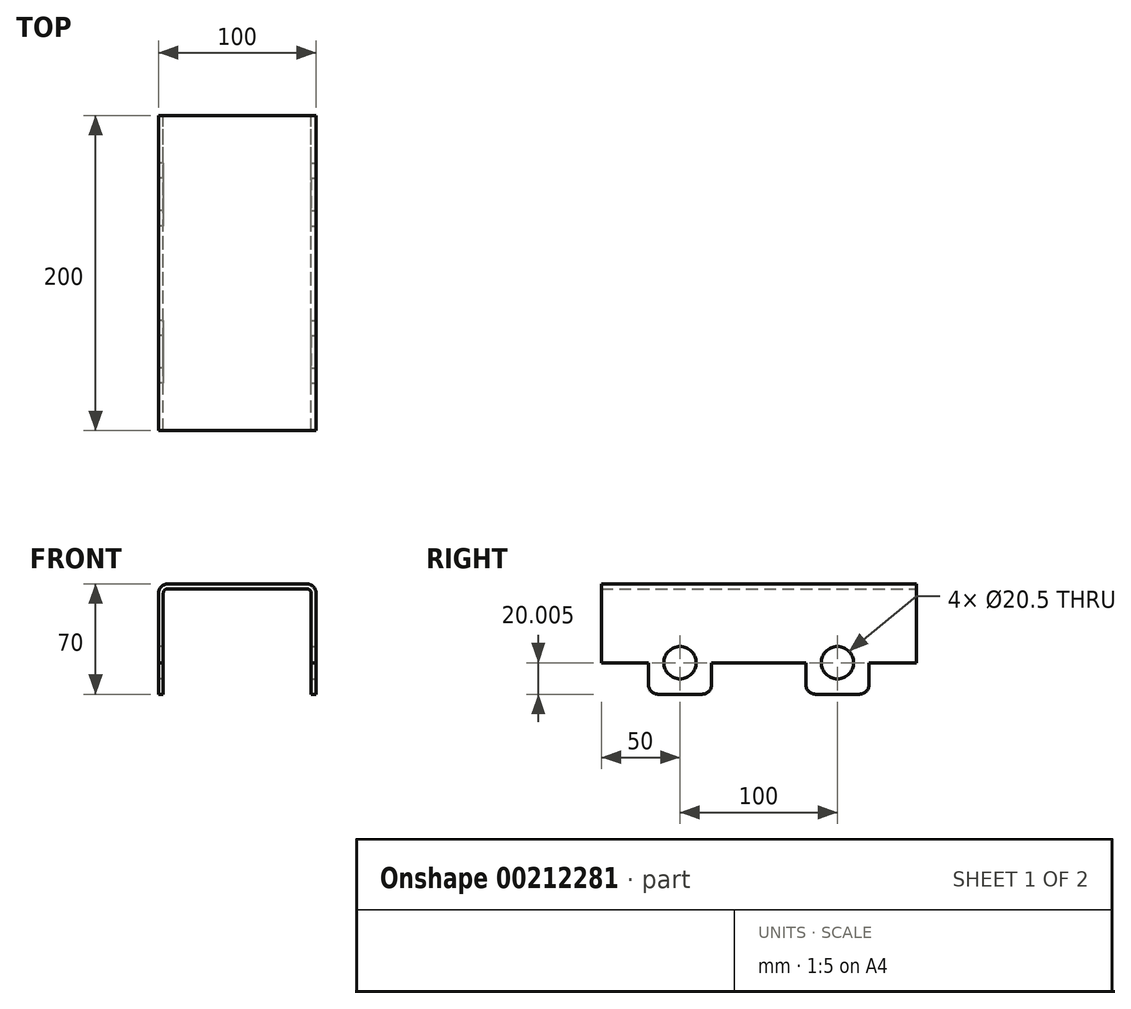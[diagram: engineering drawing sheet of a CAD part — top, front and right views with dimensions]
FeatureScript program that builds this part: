
annotation { "Feature Type Name" : "Feature", "Feature Type Description" : "" }
export const myFeature = defineFeature(function(context is Context, id is Id, definition is map)
    precondition{}
    {
        {
            var Q0;
            Q0=qCreatedBy(makeId("Front.planeOp"),FACE);
            var sketch = newSketch(context, id + "F0", { "sketchPlane" : qUnion([Q0])});
            skLineSegment(sketch, "E0", {"start": v(0, 20.85) * mm, "end": v(44, 20.85) * mm});
            skLineSegment(sketch, "E1", {"start": v(47, 17.85) * mm, "end": v(47, -26.15) * mm});
            skLineSegment(sketch, "E2", {"start": v(47, -26.15) * mm, "end": v(50, -26.15) * mm});
            skLineSegment(sketch, "E3", {"start": v(50, -26.15) * mm, "end": v(50, 17.85) * mm});
            skLineSegment(sketch, "E4", {"start": v(44, 23.85) * mm, "end": v(0, 23.85) * mm});
            skLineSegment(sketch, "E5", {"start": v(0, 20.85) * mm, "end": v(0, 23.85) * mm});
            skPoint(sketch, "E6.visualSharp", {"position": v(47, 20.85) * mm});
            skArc(sketch, "E6.filletArc", {"start": v(47, 17.85) * mm, "mid": v(46.12, 19.98) * mm, "end": v(44, 20.85) * mm});
            skPoint(sketch, "E7.visualSharp", {"position": v(50, 23.85) * mm});
            skArc(sketch, "E7.filletArc", {"start": v(50, 17.85) * mm, "mid": v(48.24, 22.1) * mm, "end": v(44, 23.85) * mm});
            skLineSegment(sketch, "E8.MirrorCS", {"start": v(-47, -26.15) * mm, "end": v(-50, -26.15) * mm});
            skArc(sketch, "E9.MirrorCS", {"start": v(-47, 17.85) * mm, "mid": v(-46.12, 19.98) * mm, "end": v(-44, 20.85) * mm});
            skLineSegment(sketch, "E10.MirrorCS", {"start": v(0, 20.85) * mm, "end": v(-44, 20.85) * mm});
            skLineSegment(sketch, "E11.MirrorCS", {"start": v(-47, 17.85) * mm, "end": v(-47, -26.15) * mm});
            skLineSegment(sketch, "E12.MirrorCS", {"start": v(-44, 23.85) * mm, "end": v(0, 23.85) * mm});
            skPoint(sketch, "E13.MirrorP", {"position": v(-47, 20.85) * mm});
            skPoint(sketch, "E14.MirrorP", {"position": v(-50, 23.85) * mm});
            skArc(sketch, "E15.MirrorCS", {"start": v(-50, 17.85) * mm, "mid": v(-48.24, 22.1) * mm, "end": v(-44, 23.85) * mm});
            skLineSegment(sketch, "E16.MirrorCS", {"start": v(-50, -26.15) * mm, "end": v(-50, 17.85) * mm});
            skSolve(sketch);
        }
        {
            var Q0;
            Q0=makeQuery(id+"F0.imprint","IMPRINT",FACE,{"disambiguationData":[TD([[makeQuery(id+"F0.imprint","IMPRINT",EDGE,{"derivedFrom":sQuery(id+"F0.wireOp",EDGE,"E0")}),1.0]])]});
            var Q1;
            Q1=makeQuery(id+"F0.imprint","IMPRINT",FACE,{"disambiguationData":[TD([[makeQuery(id+"F0.imprint","IMPRINT",EDGE,{"derivedFrom":sQuery(id+"F0.wireOp",EDGE,"E5")}),1.0]])]});
            extrude(context, id + "F1", {"entities" : qUnion([Q0, Q1]), "depth" : 200 * mm});
        }
        {
            var Q0;
            Q0=makeQuery(id+"F1.opExtrude","SWEPT_FACE",FACE,{"disambiguationData":[OSD([sQuery(id+"F0.wireOp",EDGE,"E3")])]});
            var sketch = newSketch(context, id + "F2", { "sketchPlane" : qUnion([Q0])});
            skLineSegment(sketch, "E17.bottom", {"start": v(-170, -26.15) * mm, "end": v(-130, -26.15) * mm});
            skLineSegment(sketch, "E17.top", {"start": v(-164, -46.15) * mm, "end": v(-136, -46.15) * mm});
            skLineSegment(sketch, "E17.left", {"start": v(-170, -26.15) * mm, "end": v(-170, -40.15) * mm});
            skLineSegment(sketch, "E17.right", {"start": v(-130, -26.15) * mm, "end": v(-130, -40.15) * mm});
            skLineSegment(sketch, "E18.bottom", {"start": v(-70, -26.15) * mm, "end": v(-30, -26.15) * mm});
            skLineSegment(sketch, "E18.top", {"start": v(-64, -46.15) * mm, "end": v(-36, -46.15) * mm});
            skLineSegment(sketch, "E18.left", {"start": v(-70, -26.15) * mm, "end": v(-70, -40.15) * mm});
            skLineSegment(sketch, "E18.right", {"start": v(-30, -26.15) * mm, "end": v(-30, -40.15) * mm});
            skPoint(sketch, "E19.visualSharp", {"position": v(-170, -46.15) * mm});
            skArc(sketch, "E19.filletArc", {"start": v(-170, -40.15) * mm, "mid": v(-168.24, -44.39) * mm, "end": v(-164, -46.15) * mm});
            skPoint(sketch, "E20.visualSharp", {"position": v(-130, -46.15) * mm});
            skArc(sketch, "E20.filletArc", {"start": v(-136, -46.15) * mm, "mid": v(-131.76, -44.39) * mm, "end": v(-130, -40.15) * mm});
            skPoint(sketch, "E21.visualSharp", {"position": v(-70, -46.15) * mm});
            skArc(sketch, "E21.filletArc", {"start": v(-70, -40.15) * mm, "mid": v(-68.24, -44.39) * mm, "end": v(-64, -46.15) * mm});
            skPoint(sketch, "E22.visualSharp", {"position": v(-30, -46.15) * mm});
            skArc(sketch, "E22.filletArc", {"start": v(-36, -46.15) * mm, "mid": v(-31.76, -44.39) * mm, "end": v(-30, -40.15) * mm});
            skCircle(sketch, "E23", {"center": v(-150, -26.15) * mm, "radius": 10.25 * mm});
            skCircle(sketch, "E24", {"center": v(-50, -26.15) * mm, "radius": 10.25 * mm});
            skSolve(sketch);
        }
        {
            var Q0;
            Q0=makeQuery(id+"F2.imprint","IMPRINT",FACE,{"disambiguationData":[TD([[makeQuery(id+"F2.imprint","IMPRINT",EDGE,{"derivedFrom":sQuery(id+"F2.wireOp",EDGE,"E17.bottom")}),-1.0]])]});
            var Q1;
            Q1=makeQuery(id+"F2.imprint","IMPRINT",FACE,{"disambiguationData":[TD([[makeQuery(id+"F2.imprint","IMPRINT",EDGE,{"derivedFrom":sQuery(id+"F2.wireOp",EDGE,"E18.bottom")}),-1.0]])]});
            extrude(context, id + "F3", {"entities" : qUnion([Q0, Q1]), "operationType" : NewBodyOperationType.ADD, "oppositeDirection" : true, "depth" : 3 * mm});
        }
        {
            var Q0;
            Q0=makeQuery(id+"F3.boolean.opBoolean","MERGE",FACE,{"derivedFrom":[makeQuery(id+"F1.opExtrude","SWEPT_FACE",FACE,{"disambiguationData":[OSD([sQuery(id+"F0.wireOp",EDGE,"E3")])]}),makeQuery(id+"F3.opExtrude","CAP_FACE",FACE,{"disambiguationData":[OSD([sQuery(id+"F2.wireOp",EDGE,"E17.bottom"),sQuery(id+"F2.wireOp",EDGE,"E17.top"),sQuery(id+"F2.wireOp",EDGE,"E17.left"),sQuery(id+"F2.wireOp",EDGE,"E17.right"),sQuery(id+"F2.wireOp",EDGE,"E19.filletArc"),sQuery(id+"F2.wireOp",EDGE,"E20.filletArc"),sQuery(id+"F2.wireOp",EDGE,"E23")])],"isStart":true}),makeQuery(id+"F3.opExtrude","CAP_FACE",FACE,{"disambiguationData":[OSD([sQuery(id+"F2.wireOp",EDGE,"E18.bottom"),sQuery(id+"F2.wireOp",EDGE,"E18.top"),sQuery(id+"F2.wireOp",EDGE,"E18.left"),sQuery(id+"F2.wireOp",EDGE,"E18.right"),sQuery(id+"F2.wireOp",EDGE,"E21.filletArc"),sQuery(id+"F2.wireOp",EDGE,"E22.filletArc"),sQuery(id+"F2.wireOp",EDGE,"E24")])],"isStart":true})]});
            var sketch = newSketch(context, id + "F4", { "sketchPlane" : qUnion([Q0])});
            skCircle(sketch, "E25", {"center": v(-150, -26.15) * mm, "radius": 10.25 * mm});
            skCircle(sketch, "E26", {"center": v(-50, -26.15) * mm, "radius": 10.25 * mm});
            skSolve(sketch);
        }
        {
            var Q0;
            {var subQ1=sQuery(id+"F2.wireOp",EDGE,"E23");var subQ2=sQuery(id+"F0.wireOp",EDGE,"E3");var subQ3=sQuery(id+"F0.wireOp",EDGE,"E2");var subQ4=makeQuery(id+"F3.boolean.opBoolean","SPLIT",EDGE,{"disambiguationData":[TD([makeQuery(id+"F3.opExtrude","SWEPT_FACE",FACE,{"disambiguationData":[OSD([subQ1])]})])],"derivedFrom":makeQuery(id+"F1.opExtrude","SWEPT_EDGE",EDGE,{"disambiguationData":[OSD([subQ3,subQ2])]})});Q0=makeQuery(id+"F4.imprint","IMPRINT",FACE,{"disambiguationData":[TD([[makeQuery(id+"F4.imprint","IMPRINT",EDGE,{"derivedFrom":subQ4}),1.0]])]});}
            var Q1;
            {var subQ1=sQuery(id+"F2.wireOp",EDGE,"E24");var subQ2=sQuery(id+"F0.wireOp",EDGE,"E3");var subQ3=sQuery(id+"F0.wireOp",EDGE,"E2");var subQ4=makeQuery(id+"F3.boolean.opBoolean","SPLIT",EDGE,{"disambiguationData":[TD([makeQuery(id+"F3.opExtrude","SWEPT_FACE",FACE,{"disambiguationData":[OSD([subQ1])]})])],"derivedFrom":makeQuery(id+"F1.opExtrude","SWEPT_EDGE",EDGE,{"disambiguationData":[OSD([subQ3,subQ2])]})});Q1=makeQuery(id+"F4.imprint","IMPRINT",FACE,{"disambiguationData":[TD([[makeQuery(id+"F4.imprint","IMPRINT",EDGE,{"derivedFrom":subQ4}),1.0]])]});}
            extrude(context, id + "F5", {"entities" : qUnion([Q0, Q1]), "operationType" : NewBodyOperationType.REMOVE, "oppositeDirection" : true, "depth" : 3 * mm});
        }
        {
            var Q0;
            Q0=makeQuery(id+"F1.opExtrude","SWEPT_FACE",FACE,{"disambiguationData":[OSD([sQuery(id+"F0.wireOp",EDGE,"E16.MirrorCS")])]});
            var sketch = newSketch(context, id + "F6", { "sketchPlane" : qUnion([Q0])});
            skLineSegment(sketch, "E27.bottom", {"start": v(30, -26.15) * mm, "end": v(70, -26.15) * mm});
            skLineSegment(sketch, "E27.top", {"start": v(36, -46.15) * mm, "end": v(64, -46.15) * mm});
            skLineSegment(sketch, "E27.left", {"start": v(30, -26.15) * mm, "end": v(30, -40.15) * mm});
            skLineSegment(sketch, "E27.right", {"start": v(70, -26.15) * mm, "end": v(70, -40.15) * mm});
            skLineSegment(sketch, "E28.bottom", {"start": v(130, -26.15) * mm, "end": v(170, -26.15) * mm});
            skLineSegment(sketch, "E28.top", {"start": v(136, -46.15) * mm, "end": v(164, -46.15) * mm});
            skLineSegment(sketch, "E28.left", {"start": v(130, -26.15) * mm, "end": v(130, -40.15) * mm});
            skLineSegment(sketch, "E28.right", {"start": v(170, -26.15) * mm, "end": v(170, -40.15) * mm});
            skCircle(sketch, "E29", {"center": v(50, -26.15) * mm, "radius": 10.25 * mm});
            skCircle(sketch, "E30", {"center": v(150, -26.15) * mm, "radius": 10.25 * mm});
            skPoint(sketch, "E31.visualSharp", {"position": v(30, -46.15) * mm});
            skArc(sketch, "E31.filletArc", {"start": v(30, -40.15) * mm, "mid": v(31.76, -44.39) * mm, "end": v(36, -46.15) * mm});
            skPoint(sketch, "E32.visualSharp", {"position": v(70, -46.15) * mm});
            skArc(sketch, "E32.filletArc", {"start": v(64, -46.15) * mm, "mid": v(68.24, -44.39) * mm, "end": v(70, -40.15) * mm});
            skPoint(sketch, "E33.visualSharp", {"position": v(130, -46.15) * mm});
            skArc(sketch, "E33.filletArc", {"start": v(130, -40.15) * mm, "mid": v(131.76, -44.39) * mm, "end": v(136, -46.15) * mm});
            skPoint(sketch, "E34.visualSharp", {"position": v(170, -46.15) * mm});
            skArc(sketch, "E34.filletArc", {"start": v(164, -46.15) * mm, "mid": v(168.24, -44.39) * mm, "end": v(170, -40.15) * mm});
            skSolve(sketch);
        }
        {
            var Q0;
            {var subQ0=sQuery(id+"F6.wireOp",EDGE,"E29");var subQ1=sQuery(id+"F6.wireOp",EDGE,"E27.bottom");var subQ2=makeQuery(id+"F6.imprint","INTERSECT",VERTEX,{"disambiguationData":[OD(0.0)],"derivedFrom":[subQ1,subQ0]});Q0=makeQuery(id+"F6.imprint","IMPRINT",FACE,{"disambiguationData":[TD([[makeQuery(id+"F6.imprint","IMPRINT",EDGE,{"disambiguationData":[TD([[subQ2,-1.0]])],"derivedFrom":subQ1}),-1.0]])]});}
            var Q1;
            {var subQ0=sQuery(id+"F6.wireOp",EDGE,"E30");var subQ1=sQuery(id+"F6.wireOp",EDGE,"E28.bottom");var subQ2=makeQuery(id+"F6.imprint","INTERSECT",VERTEX,{"disambiguationData":[OD(0.0)],"derivedFrom":[subQ1,subQ0]});Q1=makeQuery(id+"F6.imprint","IMPRINT",FACE,{"disambiguationData":[TD([[makeQuery(id+"F6.imprint","IMPRINT",EDGE,{"disambiguationData":[TD([[subQ2,-1.0]])],"derivedFrom":subQ1}),-1.0]])]});}
            extrude(context, id + "F7", {"entities" : qUnion([Q0, Q1]), "operationType" : NewBodyOperationType.REMOVE, "oppositeDirection" : true, "depth" : 3 * mm});
        }
        {
            var Q0;
            Q0=makeQuery(id+"F6.imprint","IMPRINT",FACE,{"disambiguationData":[TD([[makeQuery(id+"F6.imprint","IMPRINT",EDGE,{"derivedFrom":sQuery(id+"F6.wireOp",EDGE,"E27.top")}),1.0]])]});
            var Q1;
            Q1=makeQuery(id+"F6.imprint","IMPRINT",FACE,{"disambiguationData":[TD([[makeQuery(id+"F6.imprint","IMPRINT",EDGE,{"derivedFrom":sQuery(id+"F6.wireOp",EDGE,"E28.top")}),1.0]])]});
            extrude(context, id + "F8", {"entities" : qUnion([Q0, Q1]), "operationType" : NewBodyOperationType.ADD, "oppositeDirection" : true, "depth" : 3 * mm});
        }
    });
